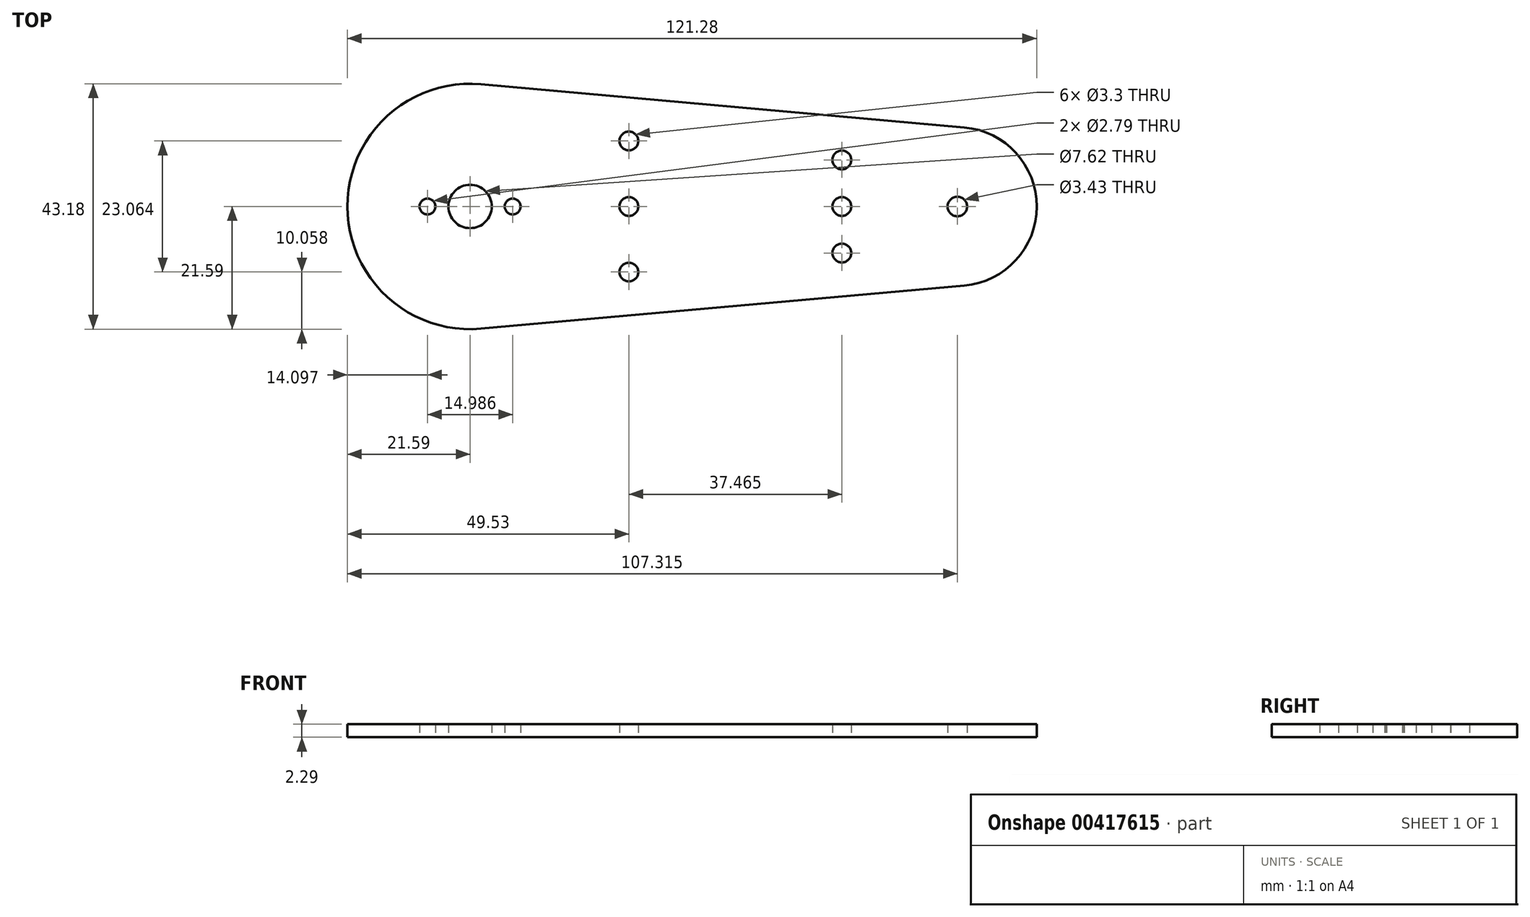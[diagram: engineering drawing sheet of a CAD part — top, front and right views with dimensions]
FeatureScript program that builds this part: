
annotation { "Feature Type Name" : "Feature", "Feature Type Description" : "" }
export const myFeature = defineFeature(function(context is Context, id is Id, definition is map)
    precondition{}
    {
        {
            var Q0;
            Q0=qCreatedBy(makeId("Top.planeOp"),FACE);
            var sketch = newSketch(context, id + "F0", { "sketchPlane" : qUnion([Q0])});
            skCircle(sketch, "E0", {"center": v(0, 0) * mm, "radius": 21.59 * mm});
            skCircle(sketch, "E1", {"center": v(85.73, 0) * mm, "radius": 13.97 * mm});
            skLineSegment(sketch, "E2", {"start": v(86.97, 13.91) * mm, "end": v(1.92, 21.5) * mm});
            skLineSegment(sketch, "E3", {"start": v(1.92, -21.5) * mm, "end": v(86.97, -13.91) * mm});
            skCircle(sketch, "E4", {"center": v(85.73, 0) * mm, "radius": 1.71 * mm});
            skCircle(sketch, "E5", {"center": v(0, 0) * mm, "radius": 3.81 * mm});
            skLineSegment(sketch, "E6.0", {"start": v(0, -14.03) * mm, "end": v(85.73, -6.38) * mm, "construction": true});
            skLineSegment(sketch, "E7.0", {"start": v(85.73, 6.38) * mm, "end": v(0, 14.03) * mm, "construction": true});
            skCircle(sketch, "E8", {"center": v(27.94, 11.53) * mm, "radius": 1.65 * mm});
            skCircle(sketch, "E9", {"center": v(65.4, 8.19) * mm, "radius": 1.65 * mm});
            skCircle(sketch, "E10", {"center": v(27.94, -11.53) * mm, "radius": 1.65 * mm});
            skCircle(sketch, "E11", {"center": v(65.4, -8.19) * mm, "radius": 1.65 * mm});
            skCircle(sketch, "E12", {"center": v(27.94, 0) * mm, "radius": 1.65 * mm});
            skCircle(sketch, "E13", {"center": v(65.4, 0) * mm, "radius": 1.65 * mm});
            skCircle(sketch, "E14", {"center": v(7.5, 0) * mm, "radius": 1.4 * mm});
            skCircle(sketch, "E15", {"center": v(-7.5, 0) * mm, "radius": 1.4 * mm});
            skSolve(sketch);
        }
        {
            var Q0;
            Q0=makeQuery(id+"F0.imprint","IMPRINT",FACE,{"disambiguationData":[TD([[makeQuery(id+"F0.imprint","IMPRINT",EDGE,{"derivedFrom":sQuery(id+"F0.wireOp",EDGE,"E5")}),-1.0]])]});
            var Q1;
            {var subQ1=sQuery(id+"F0.wireOp",EDGE,"E2");Q1=makeQuery(id+"F0.imprint","IMPRINT",FACE,{"disambiguationData":[TD([[makeQuery(id+"F0.imprint","IMPRINT",EDGE,{"derivedFrom":subQ1}),1.0]])]});}
            var Q2;
            Q2=makeQuery(id+"F0.imprint","IMPRINT",FACE,{"disambiguationData":[TD([[makeQuery(id+"F0.imprint","IMPRINT",EDGE,{"derivedFrom":sQuery(id+"F0.wireOp",EDGE,"E4")}),-1.0]])]});
            extrude(context, id + "F1", {"entities" : qUnion([Q0, Q1, Q2]), "depth" : 2.3 * mm});
        }
    });
